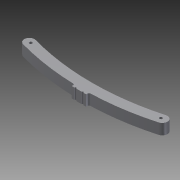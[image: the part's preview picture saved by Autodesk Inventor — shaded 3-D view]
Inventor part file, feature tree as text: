
AUTODESK INVENTOR PART (.ipt)
format: ipt  version: 2012 (Build 160160000, 160)  size: 155,136 bytes
history: native  units: in
note: dims shown in document units (in); Inventor stores cm internally (conversion verified against a paired STEP export)
features: sketch x4, fillet x3, extrude x2, hole x2, plane x2, mirror x1
ambient origin geometry x8: Origin, YZ Plane, XZ Plane, XY Plane, X Axis, Y Axis, Z Axis, Center Point
bodies: Solid1 (feature_tree)
feature tree (14):
  extrude  "Extrusion1"  Depth=1.1811in
  fillet  "Fillet1"  Radius=3.1496in
  fillet  "Fillet2"  [1 undecoded]
  hole  "Hole1"  [1 undecoded]
  plane  "Work Plane1"
  mirror  "Mirror1"
  plane  "Work Plane2"
  extrude  "Extrusion2"  Depth=0.3937in
  hole  "Hole2"  [1 undecoded]
  fillet  "Fillet3"  Radius=0.3937in
  sketch  "Sketch3"  dims[d3=15.748in d4=1.1811in d5=3.1496in d6=0.0in]
  sketch  "Sketch4"  dims[d7=0.315in d8=0.2362in d9=0.1575in d10=0.0787in d11=90.0deg d12=1.1811in d13=0.8108in d14=0.0in]
  sketch  "Sketch5"  dims[d15=0.7874in d16=0.7874in]
  sketch  "Sketch6"  dims[d17=0.5906in d18=0.0in d19=0.3937in d20=0.2756in d21=0.3937in d22=0.1969in d23=0.2362in d24=0.1575in d25=0.0787in d26=90.0deg d27=1.1811in d28=0.8108in d29=0.1614in]
note: 3 required parameter values undecoded (feature->parameter linkage not recoverable at this tier; creation-order binding heuristic only, values carry confidence <= 0.55)
